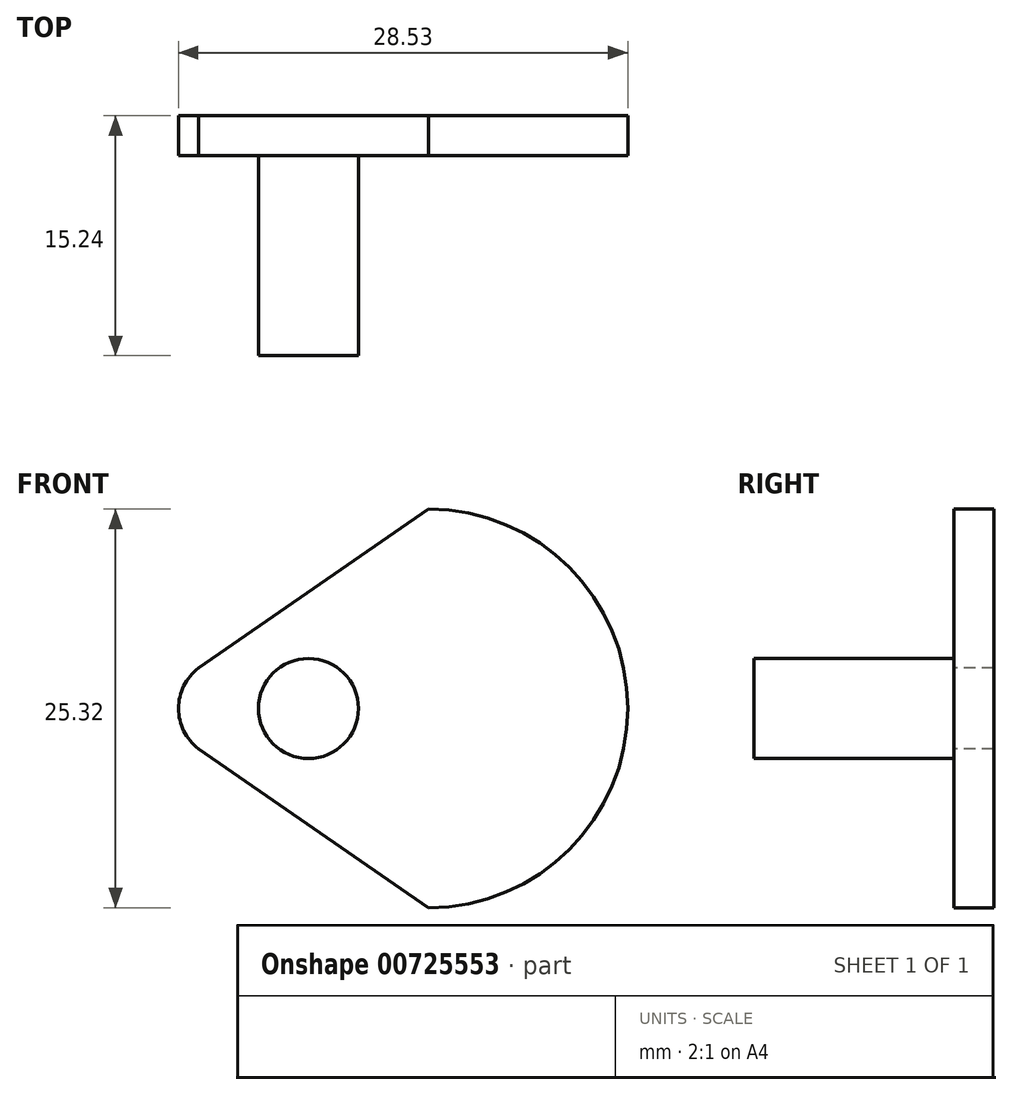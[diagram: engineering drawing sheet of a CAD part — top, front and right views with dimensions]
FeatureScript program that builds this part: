
annotation { "Feature Type Name" : "Feature", "Feature Type Description" : "" }
export const myFeature = defineFeature(function(context is Context, id is Id, definition is map)
    precondition{}
    {
        {
            var Q0;
            Q0=qCreatedBy(makeId("Front.planeOp"),FACE);
            var sketch = newSketch(context, id + "F0", { "sketchPlane" : qUnion([Q0])});
            skCircle(sketch, "E0", {"center": v(0, 0) * mm, "radius": 12.7 * mm});
            skSolve(sketch);
        }
        {
            var Q0;
            Q0=qCreatedBy(makeId("Front.planeOp"),FACE);
            var sketch = newSketch(context, id + "F1", { "sketchPlane" : qUnion([Q0])});
            skCircle(sketch, "E1", {"center": v(-7.62, 0) * mm, "radius": 3.18 * mm});
            skSolve(sketch);
        }
        {
            var Q0;
            Q0=makeQuery(id+"F1.imprint","IMPRINT",FACE,{"disambiguationData":[TD([[makeQuery(id+"F1.imprint","IMPRINT",EDGE,{"derivedFrom":sQuery(id+"F1.wireOp",EDGE,"E1")}),1.0]])]});
            extrude(context, id + "F2", {"entities" : qUnion([Q0]), "depth" : 12.7 * mm, "offsetDistance" : 25.4 * mm});
        }
        {
            var Q0;
            Q0=qCreatedBy(makeId("Front.planeOp"),FACE);
            var sketch = newSketch(context, id + "F3", { "sketchPlane" : qUnion([Q0])});
            skArc(sketch, "E2", {"start": v(0, -12.66) * mm, "mid": v(12.66, 0) * mm, "end": v(0, 12.66) * mm});
            skLineSegment(sketch, "E3", {"start": v(0, 12.66) * mm, "end": v(-14.6, 2.56) * mm});
            skArc(sketch, "E4", {"start": v(-14.6, 2.56) * mm, "mid": v(-15.87, 0) * mm, "end": v(-14.6, -2.56) * mm});
            skLineSegment(sketch, "E5", {"start": v(-14.6, -2.56) * mm, "end": v(0, -12.66) * mm});
            skSolve(sketch);
        }
        {
            var Q0;
            Q0=makeQuery(id+"F3.imprint","IMPRINT",FACE,{"disambiguationData":[TD([[makeQuery(id+"F3.imprint","IMPRINT",EDGE,{"derivedFrom":sQuery(id+"F3.wireOp",EDGE,"E2")}),1.0]])]});
            extrude(context, id + "F4", {"entities" : qUnion([Q0]), "operationType" : NewBodyOperationType.ADD, "oppositeDirection" : true, "depth" : 2.54 * mm, "offsetDistance" : 25.4 * mm});
        }
    });
